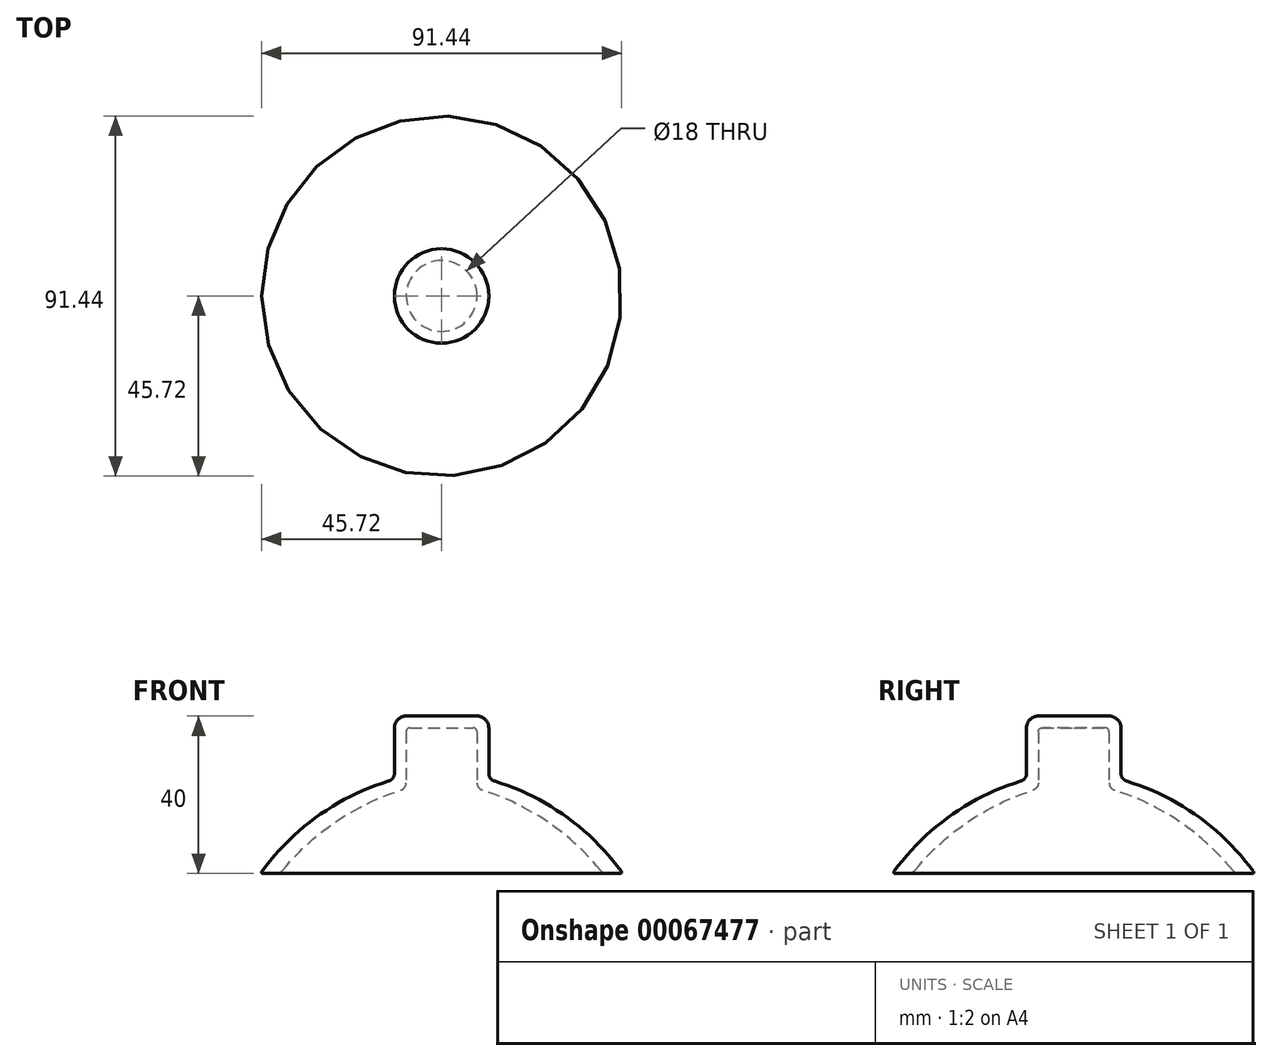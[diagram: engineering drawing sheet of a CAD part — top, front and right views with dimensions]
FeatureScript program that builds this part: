
annotation { "Feature Type Name" : "Feature", "Feature Type Description" : "" }
export const myFeature = defineFeature(function(context is Context, id is Id, definition is map)
    precondition{}
    {
        {
            var Q0;
            Q0=qCreatedBy(makeId("Front.planeOp"),FACE);
            var sketch = newSketch(context, id + "F0", { "sketchPlane" : qUnion([Q0])});
            skLineSegment(sketch, "E0", {"start": v(-46, 0) * mm, "end": v(0, 0) * mm, "construction": true});
            skLineSegment(sketch, "E1", {"start": v(0, 0) * mm, "end": v(0, 26) * mm, "construction": true});
            skLineSegment(sketch, "E2", {"start": v(0, 0) * mm, "end": v(0, 48.6) * mm, "construction": true});
            skArc(sketch, "E3", {"start": v(-13.42, 23.47) * mm, "mid": v(-31.41, 14.6) * mm, "end": v(-45.66, 0.48) * mm});
            skLineSegment(sketch, "E4", {"start": v(-46, 0) * mm, "end": v(-41, 0) * mm, "construction": true});
            skLineSegment(sketch, "E5", {"start": v(-41, 0) * mm, "end": v(-41, 0) * mm});
            skLineSegment(sketch, "E6", {"start": v(-45.42, 0) * mm, "end": v(-41.96, 0) * mm});
            skLineSegment(sketch, "E7", {"start": v(0, 26) * mm, "end": v(0, 23.5) * mm, "construction": true});
            skLineSegment(sketch, "E8", {"start": v(0, 23.5) * mm, "end": v(0, 26) * mm});
            skArc(sketch, "E9", {"start": v(-10.4, 21.14) * mm, "mid": v(-26.9, 13.13) * mm, "end": v(-40.4, 0.74) * mm});
            skLineSegment(sketch, "E10", {"start": v(-9, 26) * mm, "end": v(-12, 26) * mm});
            skLineSegment(sketch, "E11", {"start": v(-12, 26) * mm, "end": v(-12, 25.39) * mm});
            skLineSegment(sketch, "E12", {"start": v(-1.91, 25.82) * mm, "end": v(-1.92, 25.82) * mm});
            skArc(sketch, "E13.filletArc", {"start": v(-13.42, 23.47) * mm, "mid": v(-12.4, 24.2) * mm, "end": v(-12, 25.39) * mm});
            skLineSegment(sketch, "E14", {"start": v(-12, 26) * mm, "end": v(-12, 37) * mm});
            skLineSegment(sketch, "E15", {"start": v(-9, 40) * mm, "end": v(0, 40) * mm});
            skLineSegment(sketch, "E16", {"start": v(0, 40) * mm, "end": v(0, 37) * mm});
            skPoint(sketch, "E17.visualSharp", {"position": v(-12, 40) * mm});
            skArc(sketch, "E17.filletArc", {"start": v(-9, 40) * mm, "mid": v(-11.12, 39.12) * mm, "end": v(-12, 37) * mm});
            skLineSegment(sketch, "E18", {"start": v(0, 37) * mm, "end": v(-8, 37) * mm});
            skLineSegment(sketch, "E19", {"start": v(-9, 36) * mm, "end": v(-9, 23.05) * mm});
            skArc(sketch, "E20.filletArc", {"start": v(-8, 37) * mm, "mid": v(-8.7, 36.7) * mm, "end": v(-9, 36) * mm});
            skPoint(sketch, "E21.visualSharp", {"position": v(-46, 0) * mm});
            skArc(sketch, "E21.filletArc", {"start": v(-45.66, 0.48) * mm, "mid": v(-45.68, 0.16) * mm, "end": v(-45.42, 0) * mm});
            skPoint(sketch, "E22.visualSharp", {"position": v(-41, 0) * mm});
            skArc(sketch, "E22.filletArc", {"start": v(-41.96, 0) * mm, "mid": v(-41.1, 0.2) * mm, "end": v(-40.4, 0.74) * mm});
            skPoint(sketch, "E23.visualSharp", {"position": v(-9, 21.57) * mm});
            skArc(sketch, "E23.filletArc", {"start": v(-10.4, 21.14) * mm, "mid": v(-9.39, 21.87) * mm, "end": v(-9, 23.05) * mm});
            skSolve(sketch);
        }
        {
            var Q0;
            Q0=makeQuery(id+"F0.imprint","IMPRINT",FACE,{"disambiguationData":[TD([[makeQuery(id+"F0.imprint","IMPRINT",EDGE,{"derivedFrom":sQuery(id+"F0.wireOp",EDGE,"E3")}),1.0]])]});
            var Q1;
            Q1=makeQuery(id+"F0.imprint","IMPRINT",FACE,{"disambiguationData":[TD([[makeQuery(id+"F0.imprint","IMPRINT",EDGE,{"derivedFrom":sQuery(id+"F0.wireOp",EDGE,"E10")}),-1.0]])]});
            var Q2;
            Q2=sQuery(id+"F0.wireOp",EDGE,"E8");
            revolve(context, id + "F1", {"entities" : qUnion([Q0, Q1]), "axis" : qUnion([Q2]), "revolveType" : RevolveType.FULL});
        }
    });
